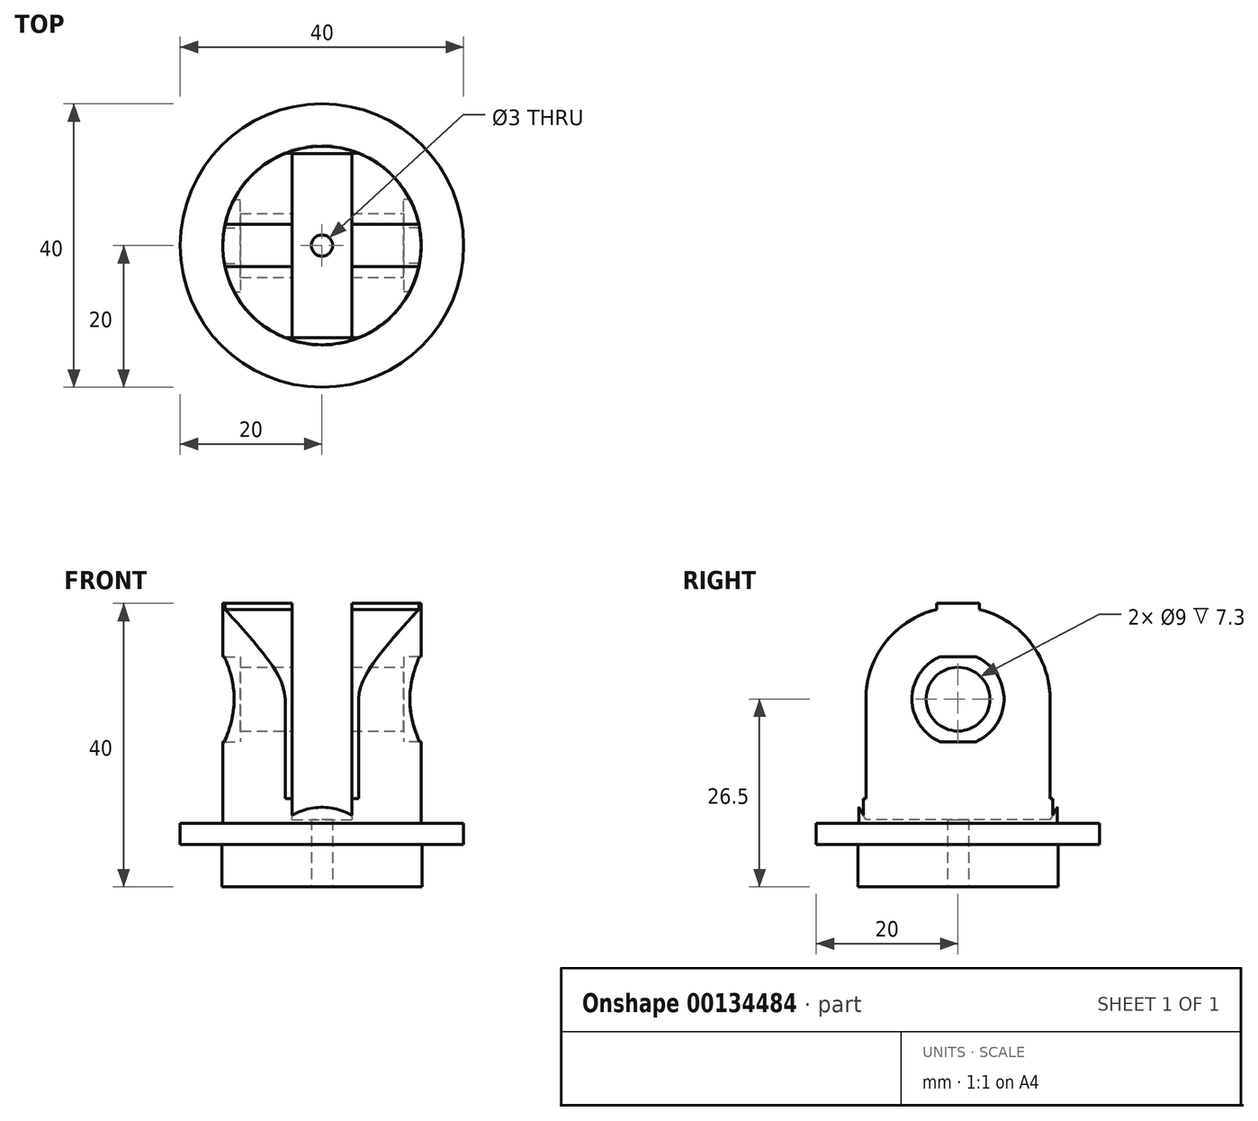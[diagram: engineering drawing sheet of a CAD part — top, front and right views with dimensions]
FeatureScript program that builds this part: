
annotation { "Feature Type Name" : "Feature", "Feature Type Description" : "" }
export const myFeature = defineFeature(function(context is Context, id is Id, definition is map)
    precondition{}
    {
        {
            var Q0;
            Q0=qCreatedBy(makeId("Top.planeOp"),FACE);
            var sketch = newSketch(context, id + "F0", { "sketchPlane" : qUnion([Q0])});
            skCircle(sketch, "E0", {"center": v(0, 0) * mm, "radius": 14.15 * mm});
            skCircle(sketch, "E1", {"center": v(0, 0) * mm, "radius": 1.5 * mm});
            skSolve(sketch);
        }
        {
            var Q0;
            Q0 = qSketchRegion(id + "F0", true);
            extrude(context, id + "F1", {"entities" : qUnion([Q0]), "depth" : 6 * mm});
        }
        {
            var Q0;
            Q0=makeQuery(id+"F1.opExtrude","CAP_FACE",FACE,{"disambiguationData":[OSD([sQuery(id+"F0.wireOp",EDGE,"E0"),sQuery(id+"F0.wireOp",EDGE,"E1")])],"isStart":false});
            var sketch = newSketch(context, id + "F2", { "sketchPlane" : qUnion([Q0])});
            skCircle(sketch, "E2.0", {"center": v(0, 0) * mm, "radius": 1.5 * mm});
            skCircle(sketch, "E3", {"center": v(0, 0) * mm, "radius": 20 * mm});
            skSolve(sketch);
        }
        {
            var Q0;
            Q0 = qSketchRegion(id + "F2", true);
            extrude(context, id + "F3", {"entities" : qUnion([Q0]), "operationType" : NewBodyOperationType.ADD, "depth" : 3 * mm});
        }
        {
            var Q0;
            Q0=makeQuery(id+"F3.opExtrude","CAP_FACE",FACE,{"disambiguationData":[OSD([sQuery(id+"F2.wireOp",EDGE,"E2.0"),sQuery(id+"F2.wireOp",EDGE,"E3")])],"isStart":false});
            var sketch = newSketch(context, id + "F4", { "sketchPlane" : qUnion([Q0])});
            skCircle(sketch, "E4", {"center": v(0, 0) * mm, "radius": 14 * mm});
            skCircle(sketch, "E5.0", {"center": v(0, 0) * mm, "radius": 1.5 * mm});
            skSolve(sketch);
        }
        {
            var Q0;
            Q0 = qSketchRegion(id + "F4", true);
            extrude(context, id + "F5", {"entities" : qUnion([Q0]), "operationType" : NewBodyOperationType.ADD, "depth" : 31 * mm});
        }
        {
            var Q0;
            Q0=qCreatedBy(makeId("Right.planeOp"),FACE);
            var sketch = newSketch(context, id + "F6", { "sketchPlane" : qUnion([Q0])});
            skCircle(sketch, "E6", {"center": v(0, 26.5) * mm, "radius": 4.5 * mm});
            skSolve(sketch);
        }
        {
            var Q0;
            Q0 = qSketchRegion(id + "F6", true);
            extrude(context, id + "F7", {"entities" : qUnion([Q0]), "operationType" : NewBodyOperationType.REMOVE, "endBound" : BoundingType.THROUGH_ALL, "oppositeDirection" : true, "depth" : 25 * mm, "hasSecondDirection" : true, "secondDirectionBound" : BoundingType.THROUGH_ALL, "secondDirectionOppositeDirection" : false, "secondDirectionDepth" : 25 * mm});
        }
        {
            var Q0;
            Q0=qCreatedBy(makeId("Right.planeOp"),FACE);
            var sketch = newSketch(context, id + "F8", { "sketchPlane" : qUnion([Q0])});
            skCircle(sketch, "E7.cCircle", {"center": v(0, 32) * mm, "radius": 22.5 * mm, "construction": true});
            skLineSegment(sketch, "E7.0", {"start": v(13, 9.5) * mm, "end": v(-13, 9.5) * mm});
            skLineSegment(sketch, "E7.1", {"start": v(-13, 9.5) * mm, "end": v(-25.98, 32) * mm});
            skLineSegment(sketch, "E7.2", {"start": v(-25.98, 32) * mm, "end": v(-13, 54.5) * mm, "construction": true});
            skLineSegment(sketch, "E7.3", {"start": v(-13, 54.5) * mm, "end": v(13, 54.5) * mm, "construction": true});
            skLineSegment(sketch, "E7.4", {"start": v(13, 54.5) * mm, "end": v(25.98, 32) * mm, "construction": true});
            skLineSegment(sketch, "E7.5", {"start": v(25.98, 32) * mm, "end": v(13, 9.5) * mm});
            skPoint(sketch, "E7.0.midPoint", {"position": v(0, 9.5) * mm});
            skCircle(sketch, "E8.0", {"center": v(0, 26.5) * mm, "radius": 4.5 * mm, "construction": true});
            skLineSegment(sketch, "E9", {"start": v(-25.98, 32) * mm, "end": v(-25.98, 52.7) * mm});
            skLineSegment(sketch, "E10", {"start": v(-25.98, 52.7) * mm, "end": v(25.98, 52.7) * mm});
            skLineSegment(sketch, "E11", {"start": v(25.98, 52.7) * mm, "end": v(25.98, 32) * mm});
            skSolve(sketch);
        }
        {
            var Q0;
            Q0 = qSketchRegion(id + "F8", true);
            extrude(context, id + "F9", {"entities" : qUnion([Q0]), "operationType" : NewBodyOperationType.REMOVE, "oppositeDirection" : true, "depth" : 8.4 * mm, "symmetric" : true});
        }
        {
            var Q0;
            Q0=qCreatedBy(makeId("Right.planeOp"),FACE);
            var sketch = newSketch(context, id + "F10", { "sketchPlane" : qUnion([Q0])});
            skLineSegment(sketch, "E12.bottom", {"start": v(-3, 43.19) * mm, "end": v(3, 43.19) * mm});
            skLineSegment(sketch, "E12.left", {"start": v(-3, 43.19) * mm, "end": v(-3, 39.15) * mm});
            skLineSegment(sketch, "E12.right", {"start": v(3, 43.19) * mm, "end": v(3, 39.15) * mm});
            skCircle(sketch, "E13.0", {"center": v(0, 26.5) * mm, "radius": 4.5 * mm, "construction": true});
            skLineSegment(sketch, "E14", {"start": v(-14, 9) * mm, "end": v(-14, 13.75) * mm, "construction": true});
            skLineSegment(sketch, "E15", {"start": v(14, 13.75) * mm, "end": v(14, 9) * mm, "construction": true});
            skArc(sketch, "E16", {"start": v(13, 26.5) * mm, "mid": v(10.2, 34.56) * mm, "end": v(3, 39.15) * mm});
            skLineSegment(sketch, "E17", {"start": v(-13, 26.5) * mm, "end": v(-13, 12.5) * mm});
            skLineSegment(sketch, "E18", {"start": v(-13, 12.5) * mm, "end": v(-17.4, 12.5) * mm});
            skLineSegment(sketch, "E19", {"start": v(-17.4, 12.5) * mm, "end": v(-17.4, 47.17) * mm});
            skLineSegment(sketch, "E20", {"start": v(-17.4, 47.17) * mm, "end": v(19.3, 47.17) * mm});
            skLineSegment(sketch, "E21", {"start": v(19.3, 47.17) * mm, "end": v(19.3, 12.5) * mm});
            skLineSegment(sketch, "E22", {"start": v(19.3, 12.5) * mm, "end": v(13, 12.5) * mm});
            skLineSegment(sketch, "E23", {"start": v(13, 12.5) * mm, "end": v(13, 26.5) * mm});
            skArc(sketch, "E24.trimOffspring", {"start": v(-3, 39.15) * mm, "mid": v(-10.2, 34.56) * mm, "end": v(-13, 26.5) * mm});
            skSolve(sketch);
        }
        {
            var Q0;
            Q0 = qSketchRegion(id + "F10", true);
            extrude(context, id + "F11", {"entities" : qUnion([Q0]), "operationType" : NewBodyOperationType.REMOVE, "endBound" : BoundingType.THROUGH_ALL, "oppositeDirection" : true, "depth" : 25 * mm, "hasSecondDirection" : true, "secondDirectionBound" : BoundingType.THROUGH_ALL, "secondDirectionOppositeDirection" : false, "secondDirectionDepth" : 25 * mm});
        }
        {
            var Q0;
            Q0=qCreatedBy(makeId("Right.planeOp"),FACE);
            cPlane(context, id + "F12", {"entities" : qUnion([Q0]), "cplaneType" : CPlaneType.OFFSET, "offset" : 11.5 * mm, "width" : 150 * mm, "height" : 150 * mm});
        }
        {
            var Q0;
            Q0=qCreatedBy(id+"F12.planeOp",FACE);
            var sketch = newSketch(context, id + "F13", { "sketchPlane" : qUnion([Q0])});
            skArc(sketch, "E25.0", {"start": v(-2.5, 32.5) * mm, "mid": v(-6.5, 26.5) * mm, "end": v(-2.5, 20.5) * mm});
            skLineSegment(sketch, "E26.bottom", {"start": v(2.5, 20.5) * mm, "end": v(-2.5, 20.5) * mm});
            skLineSegment(sketch, "E26.top", {"start": v(2.5, 32.5) * mm, "end": v(-2.5, 32.5) * mm});
            skLineSegment(sketch, "E26.left", {"start": v(19.81, 20.5) * mm, "end": v(19.81, 32.5) * mm, "construction": true});
            skLineSegment(sketch, "E26.right", {"start": v(-19.81, 20.5) * mm, "end": v(-19.81, 32.5) * mm, "construction": true});
            skArc(sketch, "E27.trimOffspring", {"start": v(2.5, 20.5) * mm, "mid": v(6.5, 26.5) * mm, "end": v(2.5, 32.5) * mm});
            skSolve(sketch);
        }
        {
            var Q0;
            Q0 = qSketchRegion(id + "F13", true);
            extrude(context, id + "F14", {"entities" : qUnion([Q0]), "operationType" : NewBodyOperationType.REMOVE, "depth" : 25 * mm});
        }
        {
            var Q0;
            Q0=qCreatedBy(makeId("Right.planeOp"),FACE);
            cPlane(context, id + "F15", {"entities" : qUnion([Q0]), "cplaneType" : CPlaneType.OFFSET, "offset" : 11.5 * mm, "oppositeDirection" : true, "width" : 150 * mm, "height" : 150 * mm});
        }
        {
            var Q0;
            Q0=qCreatedBy(id+"F15.planeOp",FACE);
            var sketch = newSketch(context, id + "F16", { "sketchPlane" : qUnion([Q0])});
            skArc(sketch, "E28.0", {"start": v(-2.5, 32.5) * mm, "mid": v(-6.5, 26.5) * mm, "end": v(-2.5, 20.5) * mm});
            skLineSegment(sketch, "E28.1", {"start": v(2.5, 20.5) * mm, "end": v(-2.5, 20.5) * mm});
            skLineSegment(sketch, "E28.2", {"start": v(2.5, 32.5) * mm, "end": v(-2.5, 32.5) * mm});
            skLineSegment(sketch, "E28.3", {"start": v(19.81, 20.5) * mm, "end": v(19.81, 32.5) * mm, "construction": true});
            skLineSegment(sketch, "E28.4", {"start": v(-19.81, 20.5) * mm, "end": v(-19.81, 32.5) * mm, "construction": true});
            skPoint(sketch, "E28.5", {"position": v(0, 26.5) * mm});
            skArc(sketch, "E28.6", {"start": v(2.5, 20.5) * mm, "mid": v(6.5, 26.5) * mm, "end": v(2.5, 32.5) * mm});
            skSolve(sketch);
        }
        {
            var Q0;
            Q0 = qSketchRegion(id + "F16", true);
            extrude(context, id + "F17", {"entities" : qUnion([Q0]), "operationType" : NewBodyOperationType.REMOVE, "oppositeDirection" : true, "depth" : 25 * mm});
        }
    });
